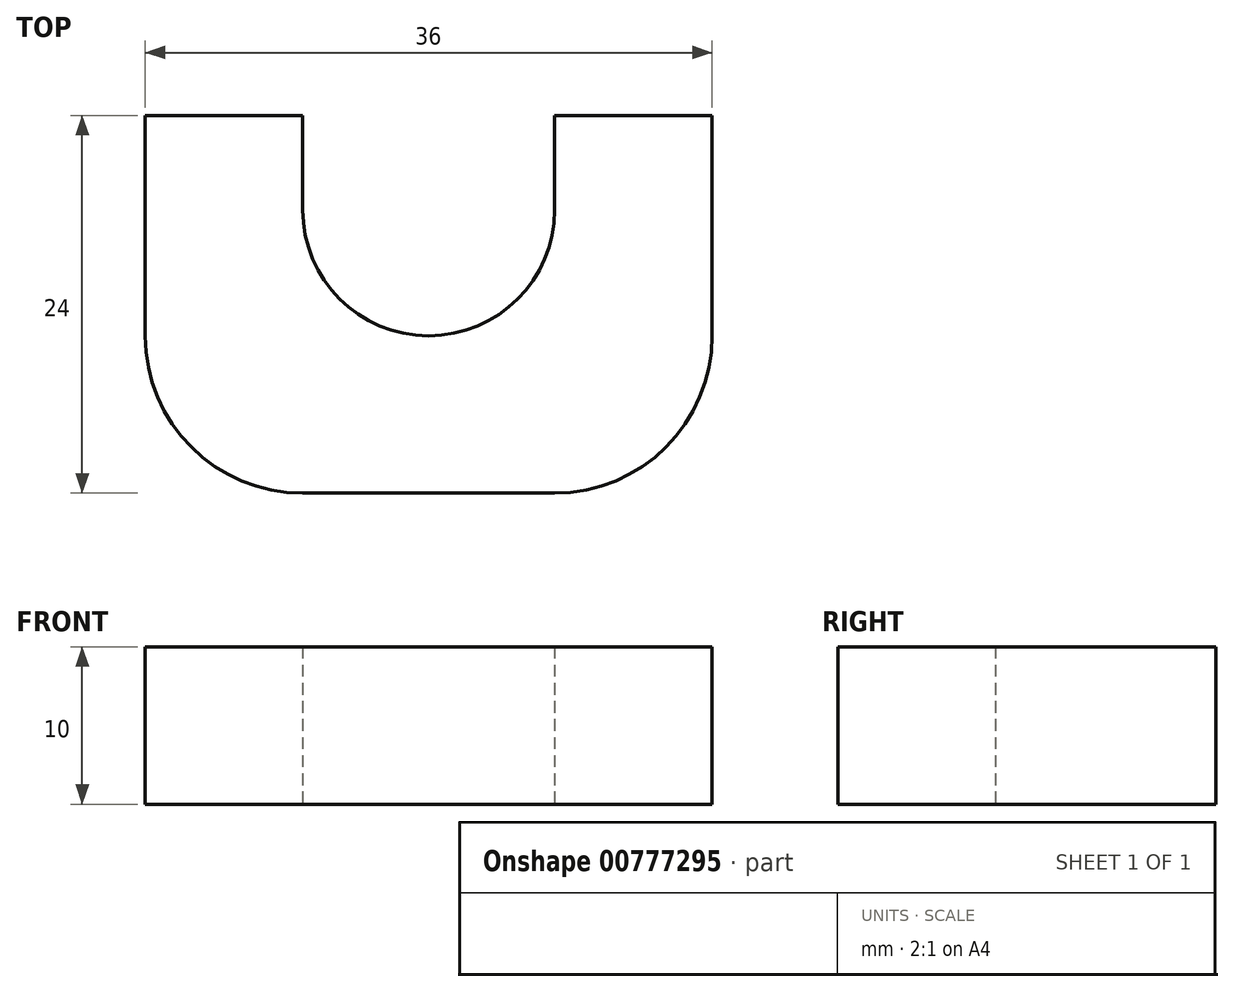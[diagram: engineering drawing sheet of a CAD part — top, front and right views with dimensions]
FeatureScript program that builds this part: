
annotation { "Feature Type Name" : "Feature", "Feature Type Description" : "" }
export const myFeature = defineFeature(function(context is Context, id is Id, definition is map)
    precondition{}
    {
        {
            var Q0;
            Q0=qCreatedBy(makeId("Top.planeOp"),FACE);
            var sketch = newSketch(context, id + "F0", { "sketchPlane" : qUnion([Q0])});
            skLineSegment(sketch, "E0.top", {"start": v(-8, -18) * mm, "end": v(8, -18) * mm});
            skLineSegment(sketch, "E0.left", {"start": v(-18, 0) * mm, "end": v(-18, -8) * mm});
            skLineSegment(sketch, "E0.right", {"start": v(18, 0) * mm, "end": v(18, -8) * mm});
            skPoint(sketch, "E1", {"position": v(-8, 0) * mm});
            skPoint(sketch, "E2", {"position": v(8, 0) * mm});
            skArc(sketch, "E3", {"start": v(-8, 0) * mm, "mid": v(0, -8) * mm, "end": v(8, 0) * mm});
            skLineSegment(sketch, "E4.top", {"start": v(-18, 6) * mm, "end": v(-8, 6) * mm});
            skLineSegment(sketch, "E4.left", {"start": v(-18, 0) * mm, "end": v(-18, 6) * mm});
            skLineSegment(sketch, "E4.right", {"start": v(-8, -0.04) * mm, "end": v(-8, 6) * mm});
            skLineSegment(sketch, "E5.top", {"start": v(8, 6) * mm, "end": v(18, 6) * mm});
            skLineSegment(sketch, "E5.left", {"start": v(8, 0) * mm, "end": v(8, 6) * mm});
            skLineSegment(sketch, "E5.right", {"start": v(18, 0) * mm, "end": v(18, 6) * mm});
            skLineSegment(sketch, "E6", {"start": v(8, 0) * mm, "end": v(8, 0) * mm});
            skPoint(sketch, "E7.visualSharp", {"position": v(-18, -18) * mm});
            skArc(sketch, "E7.filletArc", {"start": v(-18, -8) * mm, "mid": v(-15.07, -15.07) * mm, "end": v(-8, -18) * mm});
            skPoint(sketch, "E8.visualSharp", {"position": v(18, -18) * mm});
            skArc(sketch, "E8.filletArc", {"start": v(8, -18) * mm, "mid": v(15.07, -15.07) * mm, "end": v(18, -8) * mm});
            skSolve(sketch);
        }
        {
            var Q0;
            Q0=makeQuery(id+"F0.imprint","IMPRINT",FACE,{"disambiguationData":[TD([[makeQuery(id+"F0.imprint","IMPRINT",EDGE,{"derivedFrom":sQuery(id+"F0.wireOp",EDGE,"E0.top")}),1.0]])]});
            extrude(context, id + "F1", {"entities" : qUnion([Q0]), "depth" : 10 * mm, "offsetDistance" : 25 * mm});
        }
    });
